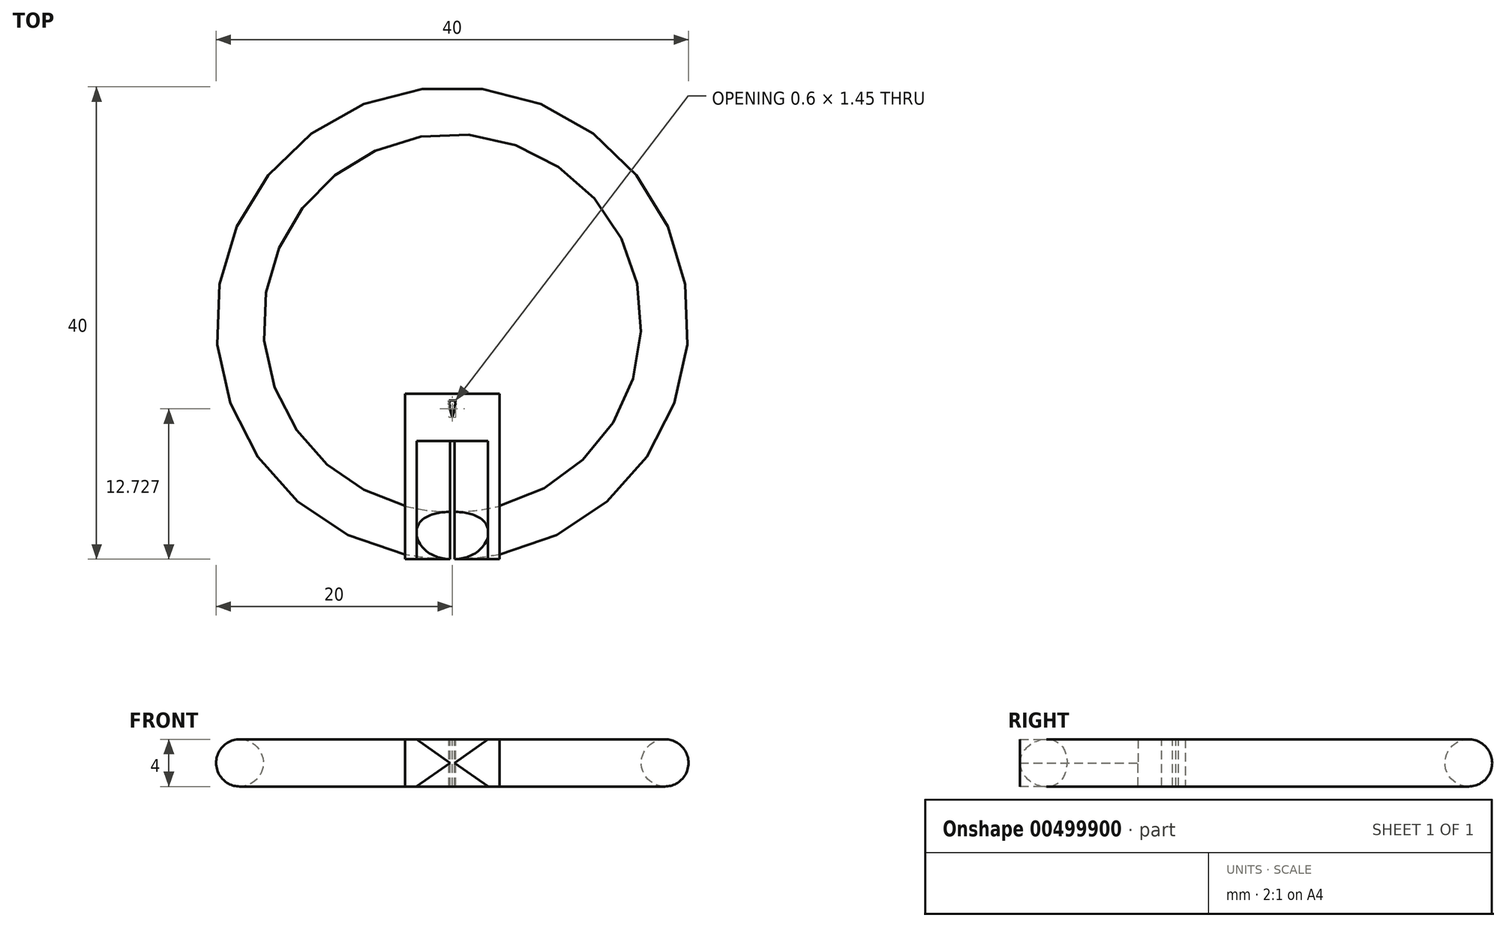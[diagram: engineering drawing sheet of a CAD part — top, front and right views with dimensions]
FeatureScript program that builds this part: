
annotation { "Feature Type Name" : "Feature", "Feature Type Description" : "" }
export const myFeature = defineFeature(function(context is Context, id is Id, definition is map)
    precondition{}
    {
        {
            var Q0;
            Q0=qCreatedBy(makeId("Top.planeOp"),FACE);
            var sketch = newSketch(context, id + "F0", { "sketchPlane" : qUnion([Q0])});
            skCircle(sketch, "E0", {"center": v(0, 0) * mm, "radius": 20 * mm});
            skCircle(sketch, "E1.0", {"center": v(0, 0) * mm, "radius": 16 * mm});
            skPoint(sketch, "E2.endSnap0", {"position": v(0, -10.39) * mm});
            skPoint(sketch, "E3.start.orphan", {"position": v(-12.17, -10.39) * mm});
            skPoint(sketch, "E4.trimOffspring.end.orphan", {"position": v(12.17, -10.39) * mm});
            skPoint(sketch, "E2.start.orphan", {"position": v(0, -20) * mm});
            skPoint(sketch, "E5.start.orphan", {"position": v(0, -6) * mm});
            skSolve(sketch);
        }
        {
            var Q0;
            Q0=qCreatedBy(makeId("Right.planeOp"),FACE);
            var sketch = newSketch(context, id + "F1", { "sketchPlane" : qUnion([Q0])});
            skPoint(sketch, "E6.center.orphan", {"position": v(9.77, 0) * mm});
            skPoint(sketch, "E7.start.orphan", {"position": v(29.77, 0) * mm});
            skCircle(sketch, "E8", {"center": v(18, 0) * mm, "radius": 2 * mm});
            skPoint(sketch, "E9.start.orphan", {"position": v(20, 0) * mm});
            skSolve(sketch);
        }
        {
            var Q0;
            Q0 = qSketchRegion(id + "F1", true);
            var Q1;
            Q1=sQuery(id+"F0.wireOp",EDGE,"E0");
            revolve(context, id + "F2", {"entities" : qUnion([Q0]), "axis" : qUnion([Q1]), "revolveType" : RevolveType.FULL});
        }
        {
            var Q0;
            Q0=qCreatedBy(makeId("Top.planeOp"),FACE);
            var sketch = newSketch(context, id + "F3", { "sketchPlane" : qUnion([Q0])});
            skLineSegment(sketch, "E10", {"start": v(4, -6) * mm, "end": v(-4, -6) * mm});
            skLineSegment(sketch, "E11", {"start": v(-4, -6) * mm, "end": v(-4, -20) * mm});
            skLineSegment(sketch, "E12", {"start": v(4, -6) * mm, "end": v(4, -20) * mm});
            skLineSegment(sketch, "E13", {"start": v(4, -20) * mm, "end": v(-4, -20) * mm});
            skSolve(sketch);
        }
        {
            var Q0;
            Q0 = qSketchRegion(id + "F3", true);
            extrude(context, id + "F4", {"entities" : qUnion([Q0]), "depth" : 2 * mm, "hasSecondDirection" : true, "secondDirectionOppositeDirection" : true, "secondDirectionDepth" : 2 * mm});
        }
        {
            var Q0;
            Q0=qCreatedBy(makeId("Front.planeOp"),FACE);
            var sketch = newSketch(context, id + "F5", { "sketchPlane" : qUnion([Q0])});
            skPoint(sketch, "E14.start.orphan", {"position": v(-3.92, -1.98) * mm});
            skLineSegment(sketch, "E15", {"start": v(-4.02, -1.98) * mm, "end": v(-3.92, -1.98) * mm});
            skLineSegment(sketch, "E16", {"start": v(0, 0) * mm, "end": v(0.2, 0) * mm});
            skLineSegment(sketch, "E17", {"start": v(0, 0) * mm, "end": v(-0.2, 0) * mm});
            skLineSegment(sketch, "E18", {"start": v(-3.02, 1.98) * mm, "end": v(-0.2, 0) * mm});
            skPoint(sketch, "E19.end.orphan", {"position": v(0.2, -0.1) * mm});
            skLineSegment(sketch, "E20.MirrorCS", {"start": v(3.02, 1.98) * mm, "end": v(0.2, 0) * mm});
            skPoint(sketch, "E21.MirrorCS.end.orphan", {"position": v(4.02, 1.98) * mm});
            skPoint(sketch, "E21.MirrorCS.start.orphan", {"position": v(3.02, 1.98) * mm});
            skPoint(sketch, "E22.start.orphan", {"position": v(-4.02, 1.98) * mm});
            skLineSegment(sketch, "E23", {"start": v(3.02, 2) * mm, "end": v(3.02, 1.98) * mm});
            skLineSegment(sketch, "E24", {"start": v(3.02, 2) * mm, "end": v(-3.02, 2) * mm});
            skLineSegment(sketch, "E25", {"start": v(-3.02, 2) * mm, "end": v(-3.02, 1.98) * mm});
            skLineSegment(sketch, "E26.MirrorCS", {"start": v(3.02, -2) * mm, "end": v(-3.02, -2) * mm});
            skLineSegment(sketch, "E27.MirrorCS", {"start": v(-3.02, -2) * mm, "end": v(-3.02, -1.98) * mm});
            skPoint(sketch, "E28.MirrorP", {"position": v(3.02, -1.98) * mm});
            skLineSegment(sketch, "E29.MirrorCS", {"start": v(3.02, -2) * mm, "end": v(3.02, -1.98) * mm});
            skLineSegment(sketch, "E30.MirrorCS", {"start": v(3.02, -1.98) * mm, "end": v(0.2, 0) * mm});
            skLineSegment(sketch, "E31.MirrorCS", {"start": v(-3.02, -1.98) * mm, "end": v(-0.2, 0) * mm});
            skPoint(sketch, "E32.MirrorCS.end.orphan", {"position": v(0.2, 0) * mm});
            skPoint(sketch, "E32.MirrorCS.start.orphan", {"position": v(2.92, -1.98) * mm});
            skPoint(sketch, "E33.start.orphan", {"position": v(-2.92, -1.98) * mm});
            skSolve(sketch);
        }
        {
            var Q0;
            Q0 = qSketchRegion(id + "F5", true);
            extrude(context, id + "F6", {"entities" : qUnion([Q0]), "operationType" : NewBodyOperationType.REMOVE, "depth" : 26 * mm, "hasSecondDirection" : true, "secondDirectionOppositeDirection" : false, "secondDirectionDepth" : 10 * mm});
        }
        {
            var Q0;
            Q0=makeQuery(id+"F4.opExtrude","CAP_FACE",FACE,{"disambiguationData":[OSD([sQuery(id+"F3.wireOp",EDGE,"E10"),sQuery(id+"F3.wireOp",EDGE,"E11"),sQuery(id+"F3.wireOp",EDGE,"E12"),sQuery(id+"F3.wireOp",EDGE,"E13")])],"isStart":false});
            var sketch = newSketch(context, id + "F7", { "sketchPlane" : qUnion([Q0])});
            skLineSegment(sketch, "E34", {"start": v(0, -6) * mm, "end": v(0, -8) * mm});
            skLineSegment(sketch, "E35", {"start": v(0, -6.55) * mm, "end": v(0.3, -6.55) * mm});
            skLineSegment(sketch, "E36", {"start": v(0.3, -6.55) * mm, "end": v(0.22, -6.8) * mm});
            skLineSegment(sketch, "E37", {"start": v(0.22, -6.8) * mm, "end": v(0.28, -6.8) * mm});
            skLineSegment(sketch, "E38", {"start": v(0.28, -6.8) * mm, "end": v(0.18, -7.05) * mm});
            skLineSegment(sketch, "E39", {"start": v(0.18, -7.05) * mm, "end": v(0.25, -7.05) * mm});
            skLineSegment(sketch, "E40", {"start": v(0.25, -7.05) * mm, "end": v(0, -8) * mm});
            skLineSegment(sketch, "E41", {"start": v(0, -8) * mm, "end": v(0, -8) * mm});
            skLineSegment(sketch, "E42.trimOffspring", {"start": v(0, -8) * mm, "end": v(0, -10) * mm});
            skLineSegment(sketch, "E43.MirrorCS", {"start": v(0, -6.55) * mm, "end": v(-0.3, -6.55) * mm});
            skLineSegment(sketch, "E44.MirrorCS", {"start": v(-0.3, -6.55) * mm, "end": v(-0.22, -6.8) * mm});
            skLineSegment(sketch, "E45.MirrorCS", {"start": v(-0.28, -6.8) * mm, "end": v(-0.18, -7.05) * mm});
            skLineSegment(sketch, "E46.MirrorCS", {"start": v(-0.25, -7.05) * mm, "end": v(0, -8) * mm});
            skLineSegment(sketch, "E47.MirrorCS", {"start": v(-0.18, -7.05) * mm, "end": v(-0.25, -7.05) * mm});
            skLineSegment(sketch, "E48.MirrorCS", {"start": v(-0.22, -6.8) * mm, "end": v(-0.28, -6.8) * mm});
            skSolve(sketch);
        }
        {
            var Q0;
            Q0 = qSketchRegion(id + "F7", true);
            extrude(context, id + "F8", {"entities" : qUnion([Q0]), "operationType" : NewBodyOperationType.REMOVE, "oppositeDirection" : true, "depth" : 25 * mm});
        }
    });
